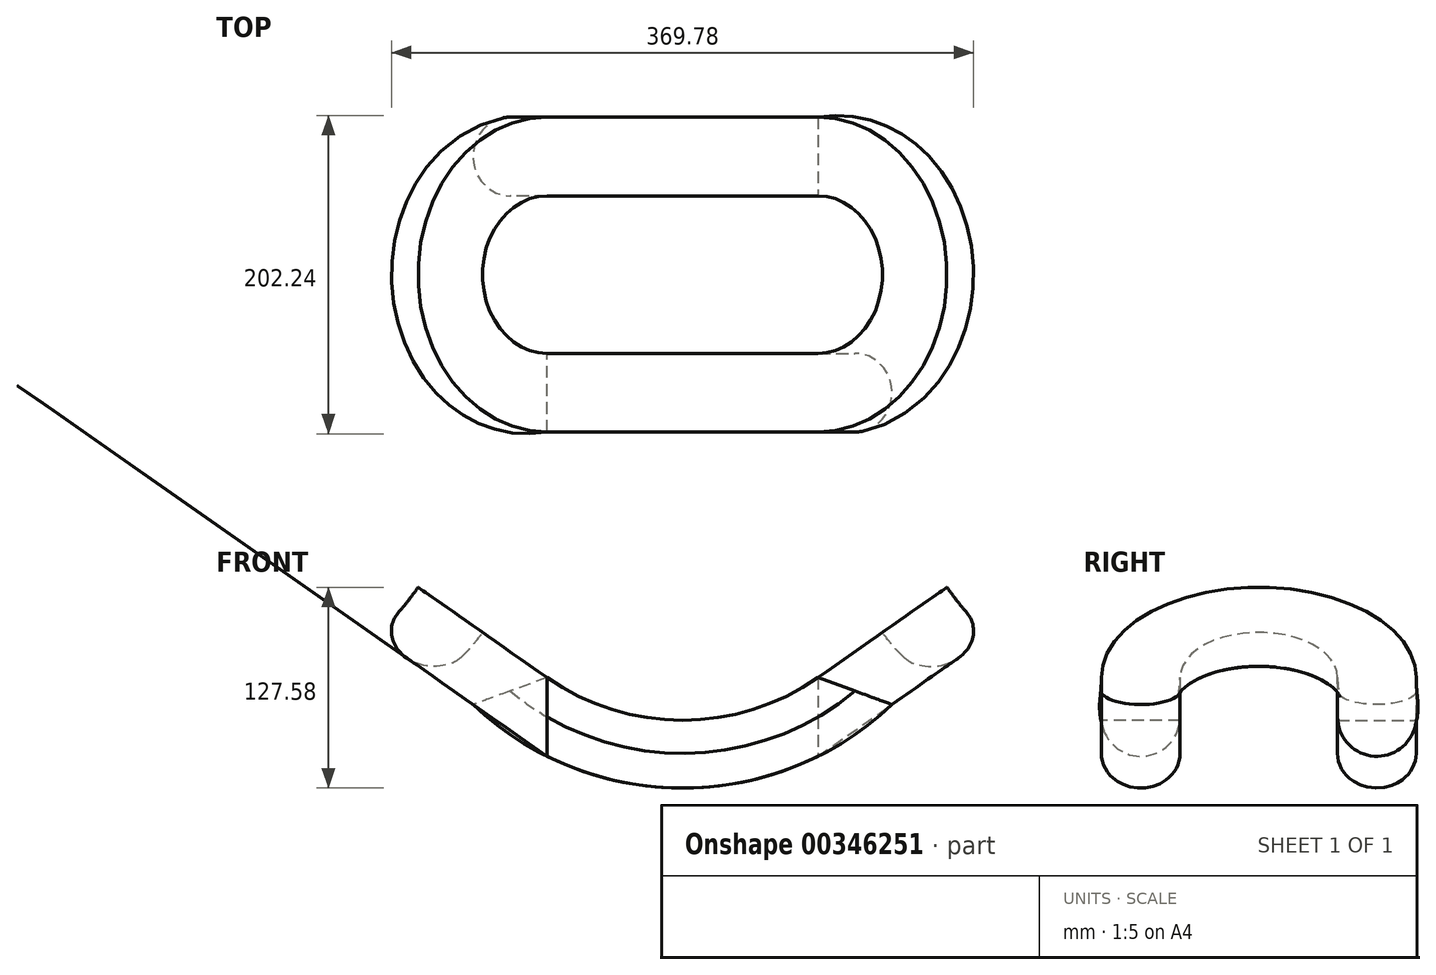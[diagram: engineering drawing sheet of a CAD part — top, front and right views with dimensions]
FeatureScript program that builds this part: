
annotation { "Feature Type Name" : "Feature", "Feature Type Description" : "" }
export const myFeature = defineFeature(function(context is Context, id is Id, definition is map)
    precondition{}
    {
        {
            var Q0;
            Q0=qCreatedBy(makeId("Front.planeOp"),FACE);
            var sketch = newSketch(context, id + "F0", { "sketchPlane" : qUnion([Q0])});
            skArc(sketch, "E0", {"start": v(-86.04, -122.87) * mm, "mid": v(0, -150) * mm, "end": v(86.04, -122.87) * mm});
            skLineSegment(sketch, "E1", {"start": v(0, 0) * mm, "end": v(0, -150) * mm});
            skLineSegment(sketch, "E2", {"start": v(0, 0) * mm, "end": v(-86.04, -122.87) * mm, "construction": true});
            skLineSegment(sketch, "E3.MirrorCS", {"start": v(0, 0) * mm, "end": v(86.04, -122.87) * mm, "construction": true});
            skLineSegment(sketch, "E4", {"start": v(-86.04, -122.87) * mm, "end": v(-226.57, -24.47) * mm});
            skLineSegment(sketch, "E5", {"start": v(86.04, -122.87) * mm, "end": v(261.52, 0) * mm});
            skSolve(sketch);
        }
        {
            var Q0;
            Q0=sQuery(id+"F0.wireOp",EDGE,"E0");
            var Q1;
            Q1=sQuery(id+"F0.wireOp",EDGE,"E5");
            var Q2;
            Q2=sQuery(id+"F0.wireOp",EDGE,"E4");
            extrude(context, id + "F1", {"bodyType" : ToolBodyType.SURFACE, "surfaceEntities" : qUnion([Q0, Q1, Q2]), "depth" : 50 * mm, "hasSecondDirection" : true, "secondDirectionOppositeDirection" : true, "secondDirectionDepth" : 50 * mm});
        }
        {
            var Q0;
            Q0=makeQuery(id+"F1.opExtrude","SWEPT_FACE",FACE,{"disambiguationData":[OSD([sQuery(id+"F0.wireOp",EDGE,"E4")])]});
            var sketch = newSketch(context, id + "F2", { "sketchPlane" : qUnion([Q0])});
            skArc(sketch, "E6", {"start": v(0, 50) * mm, "mid": v(-50, 0) * mm, "end": v(0, -50) * mm});
            skSolve(sketch);
        }
        {
            var Q0;
            Q0=makeQuery(id+"F1.opExtrude","SWEPT_FACE",FACE,{"disambiguationData":[OSD([sQuery(id+"F0.wireOp",EDGE,"E5")])]});
            var sketch = newSketch(context, id + "F3", { "sketchPlane" : qUnion([Q0])});
            skArc(sketch, "E7", {"start": v(0, -50) * mm, "mid": v(50, 0) * mm, "end": v(0, 50) * mm});
            skSolve(sketch);
        }
        {
            var Q0;
            Q0=makeQuery(id+"F1.opExtrude","SWEPT_EDGE",EDGE,{"disambiguationData":[OSD([sQuery(id+"F0.wireOp",VERTEX,"E4.start")])]});
            cPlane(context, id + "F4", {"entities" : qUnion([Q0]), "cplaneType" : CPlaneType.LINE_ANGLE, "offset" : 25 * mm, "angle" : 90 * degree, "width" : 150 * mm, "height" : 150 * mm});
        }
        {
            var Q0;
            Q0=qCreatedBy(id+"F4.planeOp",FACE);
            var sketch = newSketch(context, id + "F5", { "sketchPlane" : qUnion([Q0])});
            skLineSegment(sketch, "E8.bottom", {"start": v(-100, -122.87) * mm, "end": v(-50, -122.87) * mm});
            skLineSegment(sketch, "E8.left", {"start": v(-100, -122.87) * mm, "end": v(-100, -147.87) * mm});
            skArc(sketch, "E9", {"start": v(-100, -147.87) * mm, "mid": v(-75, -172.87) * mm, "end": v(-50, -147.87) * mm});
            skPoint(sketch, "E9.centerSnap0", {"position": v(-50, -147.87) * mm});
            skPoint(sketch, "E9.centerSnap1", {"position": v(-75, -122.87) * mm});
            skPoint(sketch, "E10.orphan", {"position": v(-50, -200) * mm});
            skLineSegment(sketch, "E11", {"start": v(-50, -122.87) * mm, "end": v(-50, -147.87) * mm});
            skSolve(sketch);
        }
        {
            var Q0;
            Q0=makeQuery(id+"F5.imprint","IMPRINT",FACE,{"disambiguationData":[TD([[makeQuery(id+"F5.imprint","IMPRINT",EDGE,{"derivedFrom":sQuery(id+"F5.wireOp",EDGE,"E8.bottom")}),-1.0]])]});
            var Q1;
            Q1=sQuery(id+"F2.wireOp",EDGE,"E6");
            var Q2;
            Q2=makeQuery(id+"F1.opExtrude","CAP_EDGE",EDGE,{"disambiguationData":[OSD([sQuery(id+"F0.wireOp",EDGE,"E0")])],"isStart":true});
            var Q3;
            Q3=sQuery(id+"F3.wireOp",EDGE,"E7");
            var Q4;
            Q4=makeQuery(id+"F1.opExtrude","CAP_EDGE",EDGE,{"disambiguationData":[OSD([sQuery(id+"F0.wireOp",EDGE,"E0")])],"isStart":false});
            sweep(context, id + "F6", {"profiles" : qUnion([Q0]), "path" : qUnion([Q1, Q2, Q3, Q4])});
        }
    });
